# Revit family: HL_Трап для балконов и террас_HL3100TK
name_source: partatom
category: Instalační zařizovací předměty
revit_build: Autodesk Revit 2016 (Build: 20151007_0715(x64)
units: mm (PartAtom-declared; Revit-internal decimal feet)

## family parameters
Bod výpočtu místnosti = Ano
Kóta kulaté spojky = Použít průměr
Nadpis OmniClass = Deck Waste Water Drains
Ořezat dutým tvarem při načtení = Ne
Sdílené = Ne
Typ součásti = Normální
Vždy vertikální = Ano
Založené na pracovní rovině = Ne
Číslo OmniClass = 23.70.50.21.24.14

## types (1)
- HL_Трап для балконов и террас_HL3100TK
    EAN = 9003076034680
    Klíčová poznámka = HL3100TK
    Komentáře k typům = Корпус для трапов для внутренних помещений DN75/110 вертикальный
    Model = HL3100TK
    Popis = Трап для балконов и террас
    Připojení CW = Ne
    Připojení HW = Ne
    Připojení odpadu = Ano
    Připojení ventilace = Ne
    URL = https://www.hutterer-lechner.com
    Výrobce = HL Hutterer & Lechner GmbH
    ВЕС = 0,5 kg
    ВЫСОТА МОНТАЖА = 163mm
    МАТЕРИАЛ = PP
    РАЗМЕР = DN 75/110
    Угол установки = 0.00°

## geometry (parser evidence)
native form markers: Blend x6, Sweep x29
no freeform markers — native parametric forms only
